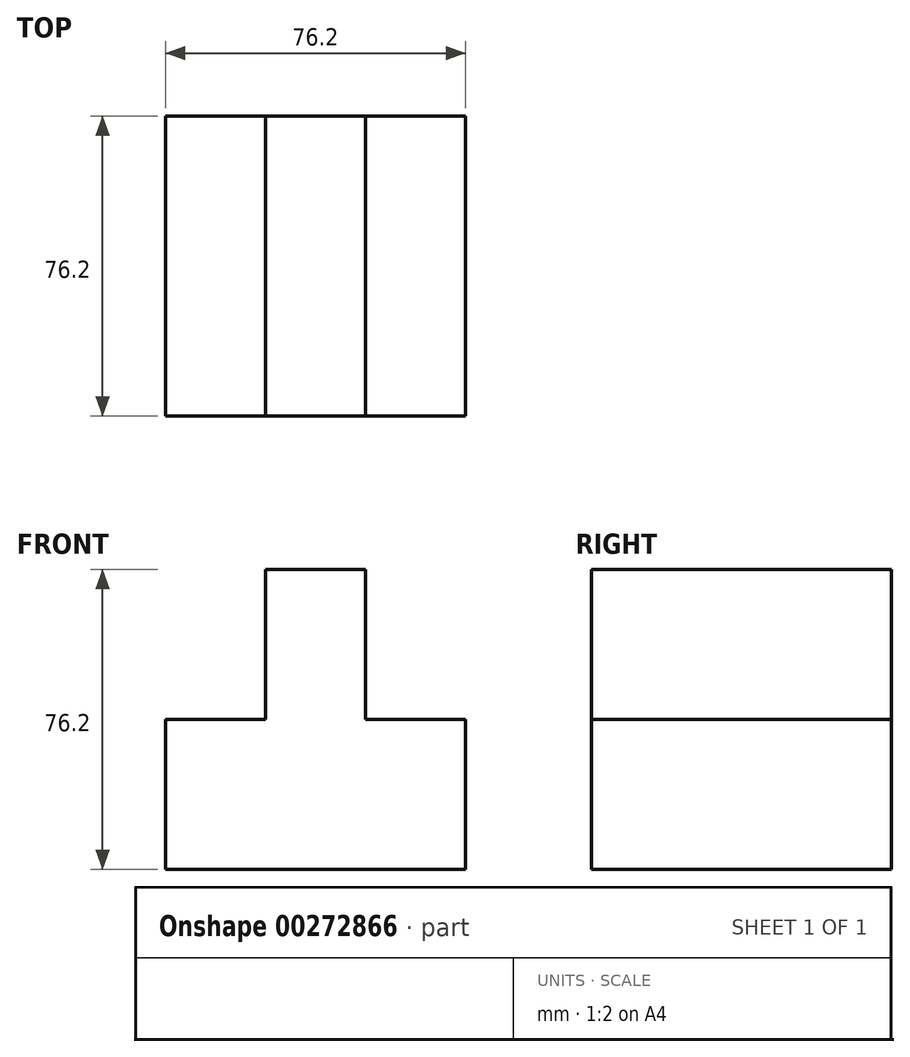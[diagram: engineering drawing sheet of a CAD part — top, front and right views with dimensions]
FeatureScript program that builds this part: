
annotation { "Feature Type Name" : "Feature", "Feature Type Description" : "" }
export const myFeature = defineFeature(function(context is Context, id is Id, definition is map)
    precondition{}
    {
        {
            var Q0;
            Q0=qCreatedBy(makeId("Front.planeOp"),FACE);
            var sketch = newSketch(context, id + "F0", { "sketchPlane" : qUnion([Q0])});
            skLineSegment(sketch, "E0", {"start": v(0, 0) * mm, "end": v(76.2, 0) * mm});
            skLineSegment(sketch, "E1", {"start": v(0, 0) * mm, "end": v(0, 38.1) * mm});
            skLineSegment(sketch, "E2", {"start": v(0, 38.1) * mm, "end": v(25.4, 38.1) * mm});
            skLineSegment(sketch, "E3", {"start": v(25.4, 38.1) * mm, "end": v(25.4, 76.2) * mm});
            skLineSegment(sketch, "E4", {"start": v(25.4, 76.2) * mm, "end": v(50.8, 76.2) * mm});
            skLineSegment(sketch, "E5", {"start": v(50.8, 76.2) * mm, "end": v(50.8, 38.1) * mm});
            skLineSegment(sketch, "E6", {"start": v(50.8, 38.1) * mm, "end": v(76.2, 38.1) * mm});
            skLineSegment(sketch, "E7", {"start": v(76.2, 38.1) * mm, "end": v(76.2, 0) * mm});
            skSolve(sketch);
        }
        {
            var Q0;
            Q0 = qSketchRegion(id + "F0", true);
            extrude(context, id + "F1", {"entities" : qUnion([Q0]), "depth" : 76.2 * mm});
        }
    });
